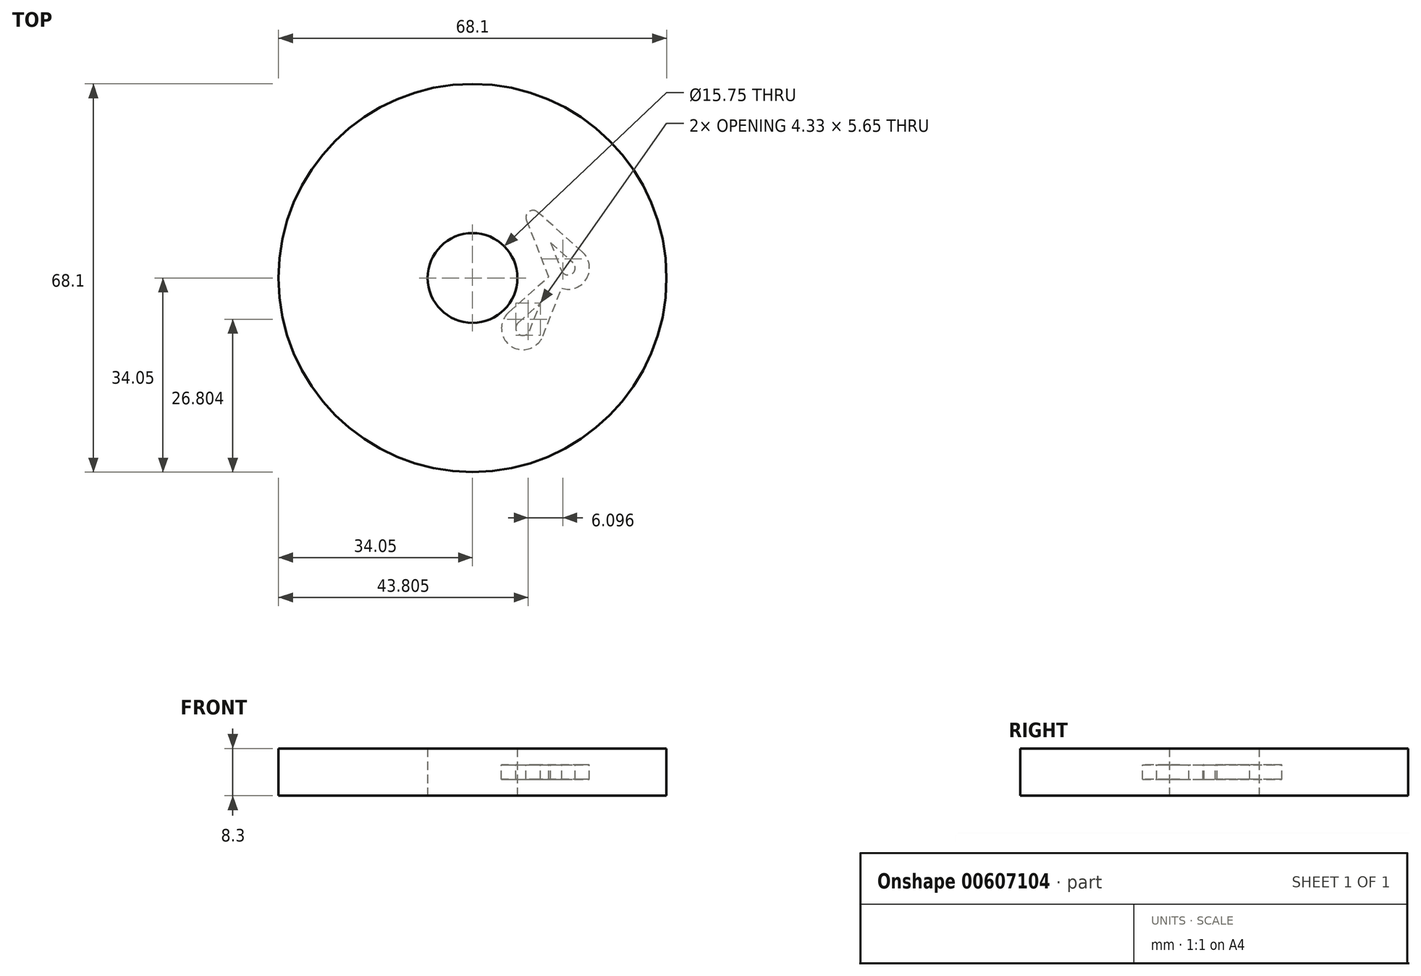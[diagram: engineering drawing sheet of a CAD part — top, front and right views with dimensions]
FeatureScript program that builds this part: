
annotation { "Feature Type Name" : "Feature", "Feature Type Description" : "" }
export const myFeature = defineFeature(function(context is Context, id is Id, definition is map)
    precondition{}
    {
        {
            var Q0;
            Q0=qCreatedBy(makeId("Top.planeOp"),FACE);
            var sketch = newSketch(context, id + "F0", { "sketchPlane" : qUnion([Q0])});
            skCircle(sketch, "E0", {"center": v(0, 0) * mm, "radius": 34.05 * mm});
            skCircle(sketch, "E1", {"center": v(0, 0) * mm, "radius": 7.88 * mm});
            skCircle(sketch, "E2", {"center": v(0, 0) * mm, "radius": 15 * mm, "construction": true});
            skLineSegment(sketch, "E3", {"start": v(-13.14, -13.14) * mm, "end": v(13.14, 13.14) * mm, "construction": true});
            skLineSegment(sketch, "E4", {"start": v(-13.14, 13.14) * mm, "end": v(13.14, -13.14) * mm, "construction": true});
            skCircle(sketch, "E5", {"center": v(10.6, 10.6) * mm, "radius": 1.25 * mm});
            skCircle(sketch, "E6", {"center": v(15, 0) * mm, "radius": 1.25 * mm});
            skCircle(sketch, "E7", {"center": v(10.6, -10.6) * mm, "radius": 1.25 * mm});
            skSolve(sketch);
        }
        {
            var Q0;
            Q0=makeQuery(id+"F0.imprint","IMPRINT",FACE,{"disambiguationData":[TD([[makeQuery(id+"F0.imprint","IMPRINT",EDGE,{"derivedFrom":sQuery(id+"F0.wireOp",EDGE,"E0")}),1.0]])]});
            var Q1;
            Q1=makeQuery(id+"F0.imprint","IMPRINT",FACE,{"disambiguationData":[TD([[makeQuery(id+"F0.imprint","IMPRINT",EDGE,{"derivedFrom":sQuery(id+"F0.wireOp",EDGE,"E5")}),1.0]])]});
            var Q2;
            Q2=makeQuery(id+"F0.imprint","IMPRINT",FACE,{"disambiguationData":[TD([[makeQuery(id+"F0.imprint","IMPRINT",EDGE,{"derivedFrom":sQuery(id+"F0.wireOp",EDGE,"E6")}),1.0]])]});
            var Q3;
            Q3=makeQuery(id+"F0.imprint","IMPRINT",FACE,{"disambiguationData":[TD([[makeQuery(id+"F0.imprint","IMPRINT",EDGE,{"derivedFrom":sQuery(id+"F0.wireOp",EDGE,"E7")}),1.0]])]});
            extrude(context, id + "F1", {"entities" : qUnion([Q0, Q1, Q2, Q3]), "endBound" : BoundingType.SYMMETRIC, "depth" : 5 * mm + 3.3 * mm, "offsetDistance" : 25 * mm});
        }
        {
            var Q0;
            Q0=qCreatedBy(makeId("Top.planeOp"),FACE);
            var sketch = newSketch(context, id + "F2", { "sketchPlane" : qUnion([Q0])});
            skArc(sketch, "E8", {"start": v(15.6, 1.31) * mm, "mid": v(17.48, 0.74) * mm, "end": v(17.6, 2.7) * mm});
            skArc(sketch, "E9", {"start": v(13.28, 0.4) * mm, "mid": v(13.32, 0.3) * mm, "end": v(13.36, 0.2) * mm});
            skArc(sketch, "E10", {"start": v(8, -7.9) * mm, "mid": v(8.12, -9.86) * mm, "end": v(10, -9.3) * mm});
            skArc(sketch, "E11", {"start": v(6.34, -6.04) * mm, "mid": v(6.7, -11.92) * mm, "end": v(12.33, -10.21) * mm});
            skLineSegment(sketch, "E12", {"start": v(6.34, -6.04) * mm, "end": v(13.36, 0.2) * mm});
            skLineSegment(sketch, "E13", {"start": v(8, -7.9) * mm, "end": v(11.92, -4.42) * mm});
            skLineSegment(sketch, "E14", {"start": v(19.26, 4.57) * mm, "end": v(11.44, 11.54) * mm});
            skLineSegment(sketch, "E15", {"start": v(10, -9.3) * mm, "end": v(11.92, -4.42) * mm});
            skLineSegment(sketch, "E16", {"start": v(12.79, -2.21) * mm, "end": v(26.65, 11.65) * mm, "construction": true});
            skCircle(sketch, "E17", {"center": v(15, 0) * mm, "radius": 1.25 * mm, "construction": true});
            skArc(sketch, "E18", {"start": v(11.44, 11.54) * mm, "mid": v(9.9, 11.63) * mm, "end": v(9.44, 10.15) * mm});
            skLineSegment(sketch, "E19", {"start": v(12.33, -10.21) * mm, "end": v(15.63, -1.8) * mm});
            skLineSegment(sketch, "E20", {"start": v(9.44, 10.15) * mm, "end": v(13.28, 0.4) * mm});
            skLineSegment(sketch, "E21.trimOffspring", {"start": v(13.69, 6.19) * mm, "end": v(17.6, 2.7) * mm});
            skLineSegment(sketch, "E22.trimOffspring", {"start": v(13.69, 6.19) * mm, "end": v(15.6, 1.31) * mm});
            skArc(sketch, "E23.trimOffspring", {"start": v(15.63, -1.8) * mm, "mid": v(20.03, -0.09) * mm, "end": v(19.26, 4.57) * mm});
            skSolve(sketch);
        }
        {
            var Q0;
            Q0 = qSketchRegion(id + "F2", true);
            extrude(context, id + "F3", {"entities" : qUnion([Q0]), "operationType" : NewBodyOperationType.REMOVE, "endBound" : BoundingType.SYMMETRIC, "oppositeDirection" : true, "depth" : 2.5 * mm, "offsetDistance" : 25 * mm});
        }
    });
